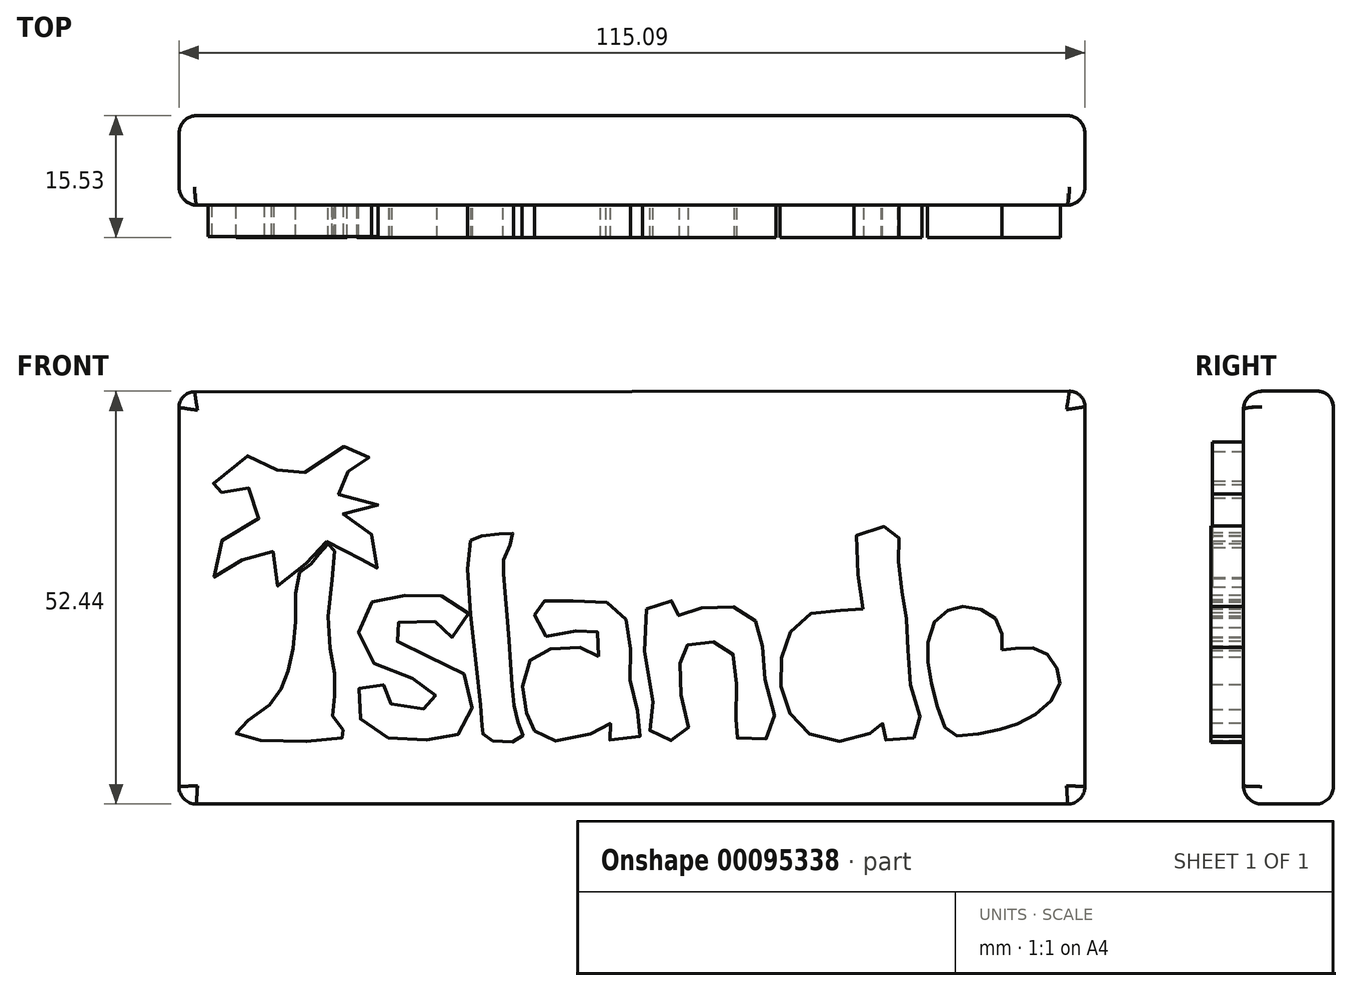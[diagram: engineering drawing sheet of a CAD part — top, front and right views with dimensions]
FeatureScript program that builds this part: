
annotation { "Feature Type Name" : "Feature", "Feature Type Description" : "" }
export const myFeature = defineFeature(function(context is Context, id is Id, definition is map)
    precondition{}
    {
        {
            var Q0;
            Q0=qCreatedBy(makeId("Front.planeOp"),FACE);
            var sketch = newSketch(context, id + "F0", { "sketchPlane" : qUnion([Q0])});
            skLineSegment(sketch, "E0", {"start": v(-58.66, 42.1) * mm, "end": v(-58.66, -10.26) * mm});
            skLineSegment(sketch, "E1", {"start": v(-58.66, -10.26) * mm, "end": v(56.43, -10.26) * mm});
            skLineSegment(sketch, "E2", {"start": v(56.43, -10.26) * mm, "end": v(56.43, 42.18) * mm});
            skLineSegment(sketch, "E3", {"start": v(56.43, 42.18) * mm, "end": v(-58.66, 42.1) * mm});
            skSolve(sketch);
        }
        {
            var Q0;
            Q0 = qSketchRegion(id + "F0", true);
            extrude(context, id + "F1", {"entities" : qUnion([Q0]), "depth" : 11.4 * mm});
        }
        {
            var Q0;
            Q0=makeQuery(id+"F1.opExtrude","CAP_FACE",FACE,{"disambiguationData":[OSD([sQuery(id+"F0.wireOp",EDGE,"E0"),sQuery(id+"F0.wireOp",EDGE,"E1"),sQuery(id+"F0.wireOp",EDGE,"E2"),sQuery(id+"F0.wireOp",EDGE,"E3")])],"isStart":false});
            var sketch = newSketch(context, id + "F2", { "sketchPlane" : qUnion([Q0])});
            skFitSpline(sketch, "E4", {"points": [v(-43.33, 19.13) * mm, v(-43.9, 11.84) * mm, v(-45.2, 5.54) * mm, v(-47.81, 1.74) * mm, v(-51.26, -1.47) * mm, v(-37.36, -1.59) * mm, v(-38.78, 0) * mm, v(-38.78, 4.47) * mm, v(-39.73, 12.67) * mm, v(-39.14, 22.76) * mm, v(-40.33, 22.29) * mm, v(-41.52, 20.5) * mm, v(-43.33, 19.13) * mm]});
            skFitSpline(sketch, "E5", {"points": [v(-26.12, 12.91) * mm, v(-25.52, 11.12) * mm, v(-21.83, 12.01) * mm, v(-22.63, 14.91) * mm, v(-25.72, 16.2) * mm, v(-30.12, 16.2) * mm, v(-33.81, 15.61) * mm, v(-35.61, 12.81) * mm, v(-35.21, 8.82) * mm, v(-30.62, 6.22) * mm, v(-26.92, 4.72) * mm, v(-25.92, 3.02) * mm, v(-26.12, 2.22) * mm, v(-30.02, 1.83) * mm, v(-31.92, 2.82) * mm, v(-32.02, 4.62) * mm, v(-34.51, 4.82) * mm, v(-35.71, 4.52) * mm, v(-35.91, 1.53) * mm, v(-34.41, -0.87) * mm, v(-29.32, -2.27) * mm, v(-25.62, -1.87) * mm, v(-22.63, -1.07) * mm, v(-21.43, 1.83) * mm, v(-22.13, 5.92) * mm, v(-26.52, 8.32) * mm, v(-30.32, 9.82) * mm, v(-31.62, 11.91) * mm, v(-30.52, 12.91) * mm, v(-26.12, 12.91) * mm]});
            skFitSpline(sketch, "E6", {"points": [v(-21.63, 23.2) * mm, v(-20.23, 1.03) * mm, v(-20.13, -1.07) * mm, v(-19.33, -2.07) * mm, v(-15.13, -1.97) * mm, v(-15.53, 0) * mm, v(-16.33, 4.72) * mm, v(-16.83, 12.01) * mm, v(-17.43, 18.8) * mm, v(-17.23, 21.4) * mm, v(-16.23, 24.1) * mm, v(-19.43, 23.8) * mm, v(-21.63, 23.2) * mm]});
            skFitSpline(sketch, "E7", {"points": [v(-5.34, 8.52) * mm, v(-7.34, 9.52) * mm, v(-12.14, 9.22) * mm, v(-14.43, 7.42) * mm, v(-14.93, 2.72) * mm, v(-13.94, 0) * mm, v(-12.84, -1.67) * mm, v(-7.24, -1.77) * mm, v(-3.85, 0) * mm, v(-4.35, -1.77) * mm, v(0, -1.57) * mm, v(-0.85, 2.72) * mm, v(-1.35, 8.22) * mm, v(-1.95, 13.31) * mm, v(-5.14, 15.51) * mm, v(-11.54, 15.41) * mm, v(-13.04, 15.31) * mm, v(-13.04, 11.61) * mm, v(-8.74, 11.51) * mm, v(-5.64, 11.81) * mm, v(-5.34, 8.52) * mm]});
            skFitSpline(sketch, "E8", {"points": [v(0.75, 14.51) * mm, v(1.55, 1.83) * mm, v(1.45, -1.47) * mm, v(5.64, -1.77) * mm, v(5.24, 3.02) * mm, v(5.14, 8.52) * mm, v(6.24, 10.12) * mm, v(10.74, 9.92) * mm, v(12.04, 7.02) * mm, v(12.04, 0) * mm, v(12.24, -1.87) * mm, v(16.73, -1.47) * mm, v(15.93, 4.62) * mm, v(15.33, 10.92) * mm, v(13.44, 14.11) * mm, v(8.04, 14.71) * mm, v(4.74, 13.71) * mm, v(4.25, 15.31) * mm, v(0.75, 14.51) * mm]});
            skFitSpline(sketch, "E9", {"points": [v(28.22, 14.51) * mm, v(24.02, 14.51) * mm, v(19.33, 12.01) * mm, v(17.73, 7.12) * mm, v(18.73, 1.63) * mm, v(22.83, -1.97) * mm, v(29.32, -1.17) * mm, v(30.72, 0) * mm, v(30.82, -1.87) * mm, v(35.31, -1.37) * mm, v(34.51, 3.72) * mm, v(33.91, 11.71) * mm, v(33.11, 17.2) * mm, v(32.72, 22.7) * mm, v(32.32, 24.5) * mm, v(27.42, 23.9) * mm, v(28.22, 14.51) * mm]});
            skFitSpline(sketch, "E10", {"points": [v(45.9, 9.32) * mm, v(45.9, 11.12) * mm, v(45.2, 13.11) * mm, v(43.5, 14.31) * mm, v(41.1, 14.81) * mm, v(39.5, 14.51) * mm, v(37.6, 13.31) * mm, v(36.51, 10.32) * mm, v(36.51, 7.52) * mm, v(37.21, 3.92) * mm, v(38.4, 0) * mm, v(39.5, -1.47) * mm, v(42.2, -1.47) * mm, v(45.8, -0.77) * mm, v(48.1, 0) * mm, v(50.8, 1.63) * mm, v(52.8, 3.82) * mm, v(53.3, 6.12) * mm, v(52.4, 7.62) * mm, v(51.1, 9.22) * mm, v(49.1, 9.62) * mm, v(47, 9.42) * mm, v(45.9, 9.32) * mm]});
            skSolve(sketch);
        }
        {
            var Q0;
            Q0 = qSketchRegion(id + "F2", true);
            extrude(context, id + "F3", {"entities" : qUnion([Q0]), "operationType" : NewBodyOperationType.ADD, "depth" : 4.13 * mm});
        }
        {
            var Q0;
            Q0=qCreatedBy(makeId("Front.planeOp"),FACE);
            var sketch = newSketch(context, id + "F4", { "sketchPlane" : qUnion([Q0])});
            skFitSpline(sketch, "E11", {"points": [v(-39.93, 23.1) * mm, v(-41.68, 22.58) * mm, v(-42.2, 20.83) * mm, v(-44.63, 18.18) * mm, v(-45.91, 17.28) * mm, v(-46.67, 19.1) * mm, v(-46.9, 21.29) * mm, v(-46.67, 22.2) * mm, v(-49.17, 21.52) * mm, v(-51.67, 20) * mm, v(-53.64, 18.49) * mm, v(-54.24, 18.64) * mm, v(-54.4, 21.21) * mm, v(-52.8, 23.64) * mm, v(-50.3, 25.38) * mm, v(-47.88, 26.51) * mm, v(-48.94, 28.7) * mm, v(-50.38, 30.52) * mm, v(-51.29, 30.68) * mm, v(-53.56, 29.09) * mm, v(-54.77, 28.63) * mm, v(-54.85, 29.7) * mm, v(-52.88, 31.58) * mm, v(-50.23, 33.78) * mm, v(-48.72, 34.46) * mm, v(-46.75, 32.87) * mm, v(-44.25, 30.3) * mm, v(-42.89, 31.66) * mm, v(-40.16, 33.78) * mm, v(-36.98, 35.52) * mm, v(-36.22, 35.67) * mm, v(-34.63, 33.93) * mm, v(-34.26, 33.1) * mm, v(-36.22, 32.8) * mm, v(-37.97, 30.83) * mm, v(-39.25, 29.16) * mm, v(-36.83, 29.09) * mm, v(-33.8, 27.88) * mm, v(-33.35, 27.72) * mm, v(-36.15, 27.2) * mm, v(-37.81, 26.51) * mm, v(-35.77, 25.53) * mm, v(-34.1, 23.79) * mm, v(-33.42, 21.52) * mm, v(-33.5, 19.77) * mm, v(-33.8, 18.34) * mm, v(-35.09, 20.23) * mm, v(-36.9, 22.35) * mm, v(-39.93, 23.1) * mm]});
            skSolve(sketch);
        }
        {
            var Q0;
            Q0 = qSketchRegion(id + "F4", true);
            extrude(context, id + "F5", {"entities" : qUnion([Q0]), "operationType" : NewBodyOperationType.ADD, "depth" : 4.14 * mm});
        }
        {
            var Q0;
            Q0 = qSketchRegion(id + "F4", true);
            extrude(context, id + "F6", {"entities" : qUnion([Q0]), "operationType" : NewBodyOperationType.ADD, "depth" : 15.37 * mm});
        }
        {
            var Q0;
            Q0=makeQuery(id+"F1.opExtrude","CAP_EDGE",EDGE,{"disambiguationData":[OSD([sQuery(id+"F0.wireOp",EDGE,"E0")])],"isStart":false});
            var Q1;
            Q1=makeQuery(id+"F1.opExtrude","CAP_EDGE",EDGE,{"disambiguationData":[OSD([sQuery(id+"F0.wireOp",EDGE,"E3")])],"isStart":false});
            var Q2;
            Q2=makeQuery(id+"F1.opExtrude","CAP_EDGE",EDGE,{"disambiguationData":[OSD([sQuery(id+"F0.wireOp",EDGE,"E2")])],"isStart":false});
            var Q3;
            Q3=makeQuery(id+"F1.opExtrude","CAP_EDGE",EDGE,{"disambiguationData":[OSD([sQuery(id+"F0.wireOp",EDGE,"E1")])],"isStart":false});
            fillet(context, id + "F7", {"entities" : qUnion([Q0, Q1, Q2, Q3]), "radius" : 2.34 * mm, "tangentPropagation" : true, "allowEdgeOverflow" : false});
        }
        {
            var Q0;
            Q0=makeQuery(id+"F1.opExtrude","SWEPT_EDGE",EDGE,{"disambiguationData":[OSD([sQuery(id+"F0.wireOp",EDGE,"E0"),sQuery(id+"F0.wireOp",EDGE,"E3")])]});
            var Q1;
            Q1=makeQuery(id+"F1.opExtrude","CAP_EDGE",EDGE,{"disambiguationData":[OSD([sQuery(id+"F0.wireOp",EDGE,"E3")])],"isStart":true});
            var Q2;
            {var subQ0=sQuery(id+"F0.wireOp",EDGE,"E3");Q2=makeQuery(id+"F7.opFillet","BLEND_EDGE",EDGE,{"blendedFrom":[makeQuery(id+"F1.opExtrude","CAP_EDGE",EDGE,{"disambiguationData":[OSD([subQ0])],"isStart":false}),makeQuery(id+"F1.opExtrude","SWEPT_FACE",FACE,{"disambiguationData":[OSD([subQ0])]})],"blendedInto":[makeQuery(id+"F1.opExtrude","SWEPT_FACE",FACE,{"disambiguationData":[OSD([subQ0])]})]});}
            var Q3;
            Q3=makeQuery(id+"F1.opExtrude","SWEPT_EDGE",EDGE,{"disambiguationData":[OSD([sQuery(id+"F0.wireOp",EDGE,"E2"),sQuery(id+"F0.wireOp",EDGE,"E3")])]});
            fillet(context, id + "F8", {"entities" : qUnion([Q0, Q1, Q2, Q3]), "radius" : 1.98 * mm, "tangentPropagation" : true, "allowEdgeOverflow" : false});
        }
        {
            var Q0;
            Q0=makeQuery(id+"F1.opExtrude","SWEPT_EDGE",EDGE,{"disambiguationData":[OSD([sQuery(id+"F0.wireOp",EDGE,"E0"),sQuery(id+"F0.wireOp",EDGE,"E1")])]});
            var Q1;
            {var subQ0=sQuery(id+"F0.wireOp",EDGE,"E1");Q1=makeQuery(id+"F7.opFillet","BLEND_EDGE",EDGE,{"blendedFrom":[makeQuery(id+"F1.opExtrude","CAP_EDGE",EDGE,{"disambiguationData":[OSD([subQ0])],"isStart":false}),makeQuery(id+"F1.opExtrude","SWEPT_FACE",FACE,{"disambiguationData":[OSD([subQ0])]})],"blendedInto":[makeQuery(id+"F1.opExtrude","SWEPT_FACE",FACE,{"disambiguationData":[OSD([subQ0])]})]});}
            var Q2;
            Q2=makeQuery(id+"F1.opExtrude","CAP_EDGE",EDGE,{"disambiguationData":[OSD([sQuery(id+"F0.wireOp",EDGE,"E1")])],"isStart":true});
            var Q3;
            Q3=makeQuery(id+"F1.opExtrude","SWEPT_EDGE",EDGE,{"disambiguationData":[OSD([sQuery(id+"F0.wireOp",EDGE,"E1"),sQuery(id+"F0.wireOp",EDGE,"E2")])]});
            fillet(context, id + "F9", {"entities" : qUnion([Q0, Q1, Q2, Q3]), "radius" : 2.2 * mm, "tangentPropagation" : true, "allowEdgeOverflow" : false});
        }
        {
            var Q0;
            Q0=makeQuery(id+"F1.opExtrude","CAP_EDGE",EDGE,{"disambiguationData":[OSD([sQuery(id+"F0.wireOp",EDGE,"E0")])],"isStart":true});
            var Q1;
            {var subQ0=sQuery(id+"F0.wireOp",EDGE,"E3");Q1=makeQuery(id+"F8.opFillet","BLEND_EDGE",EDGE,{"blendedFrom":[makeQuery(id+"F1.opExtrude","CAP_EDGE",EDGE,{"disambiguationData":[OSD([subQ0])],"isStart":true}),makeQuery(id+"F1.opExtrude","CAP_FACE",FACE,{"disambiguationData":[OSD([sQuery(id+"F0.wireOp",EDGE,"E0"),sQuery(id+"F0.wireOp",EDGE,"E1"),sQuery(id+"F0.wireOp",EDGE,"E2"),subQ0])],"isStart":true})],"blendedInto":[makeQuery(id+"F1.opExtrude","CAP_FACE",FACE,{"disambiguationData":[OSD([sQuery(id+"F0.wireOp",EDGE,"E0"),sQuery(id+"F0.wireOp",EDGE,"E1"),sQuery(id+"F0.wireOp",EDGE,"E2"),subQ0])],"isStart":true})]});}
            var Q2;
            {var subQ0=sQuery(id+"F0.wireOp",EDGE,"E1");Q2=makeQuery(id+"F9.opFillet","BLEND_EDGE",EDGE,{"blendedFrom":[makeQuery(id+"F1.opExtrude","CAP_EDGE",EDGE,{"disambiguationData":[OSD([subQ0])],"isStart":true}),makeQuery(id+"F1.opExtrude","CAP_FACE",FACE,{"disambiguationData":[OSD([sQuery(id+"F0.wireOp",EDGE,"E0"),subQ0,sQuery(id+"F0.wireOp",EDGE,"E2"),sQuery(id+"F0.wireOp",EDGE,"E3")])],"isStart":true})],"blendedInto":[makeQuery(id+"F1.opExtrude","CAP_FACE",FACE,{"disambiguationData":[OSD([sQuery(id+"F0.wireOp",EDGE,"E0"),subQ0,sQuery(id+"F0.wireOp",EDGE,"E2"),sQuery(id+"F0.wireOp",EDGE,"E3")])],"isStart":true})]});}
            var Q3;
            Q3=makeQuery(id+"F1.opExtrude","CAP_EDGE",EDGE,{"disambiguationData":[OSD([sQuery(id+"F0.wireOp",EDGE,"E2")])],"isStart":true});
            fillet(context, id + "F10", {"entities" : qUnion([Q0, Q1, Q2, Q3]), "radius" : 2.3 * mm, "tangentPropagation" : true, "allowEdgeOverflow" : false});
        }
    });
